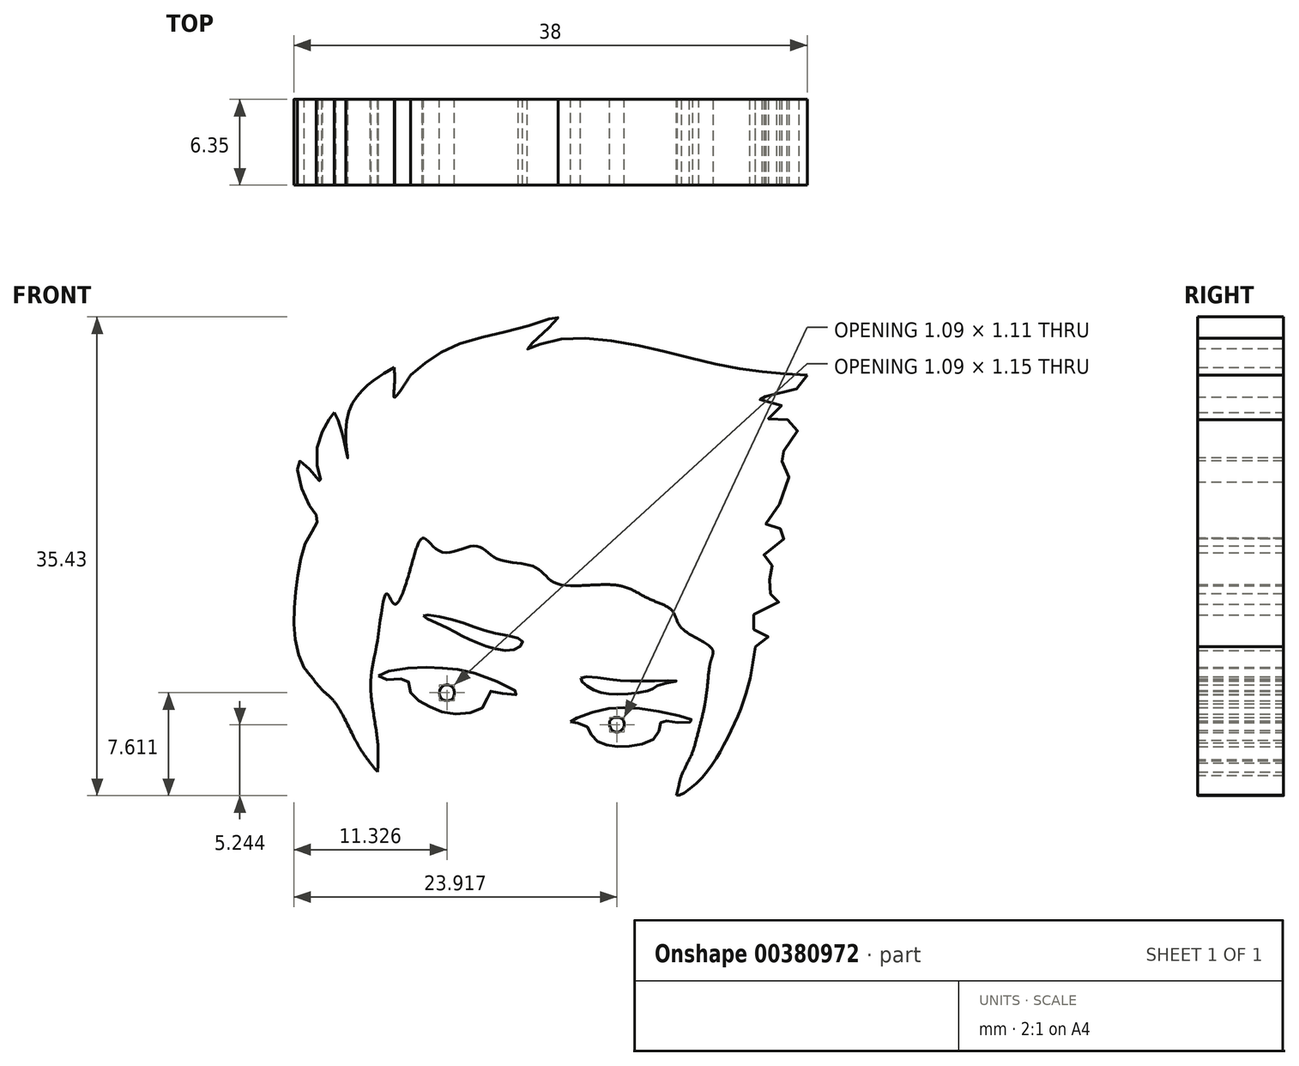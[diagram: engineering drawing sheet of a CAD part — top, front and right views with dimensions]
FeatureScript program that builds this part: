
annotation { "Feature Type Name" : "Feature", "Feature Type Description" : "" }
export const myFeature = defineFeature(function(context is Context, id is Id, definition is map)
    precondition{}
    {
        {
            var Q0;
            Q0=qCreatedBy(makeId("Front.planeOp"),FACE);
            var sketch = newSketch(context, id + "F0", { "sketchPlane" : qUnion([Q0])});
            skFitSpline(sketch, "E0", {"points": [v(-95.52, 0) * mm, v(-96.95, 1.96) * mm, v(-98.6, 5.04) * mm, v(-99.58, 6.02) * mm, v(-100.94, 7.67) * mm, v(-101.69, 10.58) * mm, v(-101.5, 13.97) * mm, v(-100.7, 17.24) * mm, v(-99.94, 18.67) * mm, v(-100.75, 20.01) * mm, v(-101.29, 23) * mm, v(-99.72, 21.44) * mm, v(-100.04, 23.01) * mm, v(-99.1, 26.1) * mm, v(-98.57, 26.77) * mm], "startDerivative": vector(-19.5, 23.13) * mm, "endDerivative": vector(11.06, 11.7) * mm});
            skFitSpline(sketch, "E1", {"points": [v(-98.73, 26.6) * mm, v(-98.23, 25.4) * mm, v(-97.73, 23.23) * mm, v(-97.79, 26.1) * mm, v(-95.96, 28.85) * mm, v(-94.28, 29.93) * mm], "startDerivative": vector(3.2, -5.81) * mm, "endDerivative": vector(8.73, 4.96) * mm});
            skFitSpline(sketch, "E2", {"points": [v(-94.28, 29.93) * mm, v(-94.28, 28.47) * mm, v(-94.28, 27.72) * mm, v(-93.08, 29.36) * mm], "startDerivative": vector(0.17, -4.17) * mm, "endDerivative": vector(3.9, 6.25) * mm});
            skFitSpline(sketch, "E3", {"points": [v(-93.08, 29.36) * mm, v(-89.77, 31.56) * mm, v(-84.03, 33.1) * mm, v(-82.17, 33.58) * mm, v(-84.45, 31.34) * mm, v(-82.96, 31.82) * mm, v(-76.32, 31.56) * mm, v(-69.24, 29.93) * mm, v(-63.71, 29.36) * mm], "startDerivative": vector(24.23, 20.38) * mm, "endDerivative": vector(37.72, -2.28) * mm});
            skFitSpline(sketch, "E4", {"points": [v(-93.6, 28.51) * mm, v(-93.08, 29.36) * mm, v(-92.1, 30.18) * mm], "startDerivative": vector(0.96, 1.87) * mm, "endDerivative": vector(2.03, 1.48) * mm});
            skFitSpline(sketch, "E5", {"points": [v(-95.52, 0) * mm, v(-95.52, 2.32) * mm, v(-96.03, 6.34) * mm, v(-95.52, 9.78) * mm, v(-94.82, 13.18) * mm, v(-94.28, 12.42) * mm, v(-93.08, 15.06) * mm, v(-92.1, 17.3) * mm, v(-90.76, 16.27) * mm, v(-88.25, 16.71) * mm, v(-86.69, 15.78) * mm, v(-83.87, 15.15) * mm, v(-82.26, 13.94) * mm, v(-77.79, 13.8) * mm, v(-75.46, 12.82) * mm, v(-73.72, 11.93) * mm, v(-73, 10.63) * mm, v(-70.77, 9.11) * mm, v(-70.86, 8.17) * mm, v(-71.22, 5.45) * mm, v(-72.29, 1.24) * mm], "startDerivative": vector(2.92, 43.61) * mm, "endDerivative": vector(-19.8, -65.15) * mm});
            skFitSpline(sketch, "E6", {"points": [v(-72.29, 1.24) * mm, v(-73.4, -1.74) * mm, v(-71.6, -0.53) * mm, v(-69.69, 2.38) * mm, v(-68.26, 5.73) * mm, v(-67.54, 9.26) * mm], "startDerivative": vector(-10.39, -20.95) * mm, "endDerivative": vector(2.54, 16.76) * mm});
            skFitSpline(sketch, "E7", {"points": [v(-63.71, 29.36) * mm, v(-64.65, 28.27) * mm, v(-67.58, 27.6) * mm, v(-65.62, 27.15) * mm, v(-66.6, 26.1) * mm, v(-64.57, 25.94) * mm, v(-64.8, 24.59) * mm, v(-65.77, 23.16) * mm, v(-65.32, 22.79) * mm, v(-65.47, 20.3) * mm, v(-66.75, 18.2) * mm, v(-65.4, 17.9) * mm, v(-65.4, 17.3) * mm, v(-67.05, 15.72) * mm, v(-66, 14.96) * mm, v(-66.9, 13.54) * mm, v(-65.62, 12.78) * mm, v(-67.8, 11.5) * mm, v(-67.65, 10.53) * mm, v(-66.6, 10) * mm, v(-67.54, 9.26) * mm], "startDerivative": vector(-8.06, -25.32) * mm, "endDerivative": vector(-34.73, -19.36) * mm});
            skFitSpline(sketch, "E8", {"points": [v(-100.94, 7.67) * mm, v(-101.6, 8.1) * mm, v(-102.13, 7.03) * mm, v(-102.24, 4.16) * mm, v(-100.94, 1.6) * mm, v(-99.36, 0) * mm, v(-96.97, -0.84) * mm, v(-96.01, -2.7) * mm, v(-93.46, -4.77) * mm, v(-89.95, -7.22) * mm, v(-88.1, -7.22) * mm, v(-87.99, -7.9) * mm, v(-85.38, -8.76) * mm, v(-81.02, -8.5) * mm, v(-80.28, -8.28) * mm, v(-79.8, -7.11) * mm, v(-78.79, -8.07) * mm, v(-75.97, -6.31) * mm, v(-74.16, -3.5) * mm, v(-73.4, -1.74) * mm, v(-72.98, -0.15) * mm, v(-72.29, 1.24) * mm, v(-71.85, 2.68) * mm, v(-71.22, 5.45) * mm, v(-70.86, 8.17) * mm, v(-70.77, 9.11) * mm, v(-73, 10.63) * mm, v(-73.72, 11.93) * mm, v(-75.46, 12.82) * mm, v(-77.79, 13.8) * mm, v(-82.26, 13.94) * mm, v(-83.87, 15.15) * mm, v(-86.69, 15.78) * mm, v(-88.25, 16.71) * mm, v(-90.76, 16.27) * mm, v(-92.1, 17.3) * mm, v(-93.08, 15.06) * mm, v(-94.28, 12.42) * mm, v(-94.82, 13.18) * mm, v(-95.52, 9.78) * mm, v(-96.03, 6.34) * mm, v(-95.52, 2.32) * mm, v(-95.47, 0.7) * mm, v(-95.52, 0) * mm, v(-96, 0.57) * mm, v(-96.95, 1.96) * mm, v(-98.6, 5.04) * mm, v(-99.58, 6.02) * mm, v(-100.94, 7.67) * mm]});
            skFitSpline(sketch, "E9", {"points": [v(-92.13, 11.55) * mm, v(-89.85, 11.24) * mm, v(-87, 10.3) * mm, v(-84.8, 9.66) * mm, v(-85.23, 9.09) * mm, v(-87.2, 9.22) * mm, v(-88.96, 9.91) * mm, v(-90.55, 10.73) * mm, v(-92.13, 11.55) * mm]});
            skFitSpline(sketch, "E10", {"points": [v(-80.46, 6.96) * mm, v(-78.33, 6.85) * mm, v(-75.65, 6.72) * mm, v(-73.34, 6.72) * mm, v(-74.83, 6.37) * mm, v(-75.3, 6.05) * mm, v(-77.46, 5.76) * mm, v(-79.08, 5.9) * mm, v(-80.22, 6.5) * mm, v(-80.46, 6.96) * mm]});
            skFitSpline(sketch, "E11", {"points": [v(-95.44, 7.1) * mm, v(-93.45, 7.67) * mm, v(-90.63, 7.67) * mm, v(-88, 7.18) * mm, v(-85.1, 5.8) * mm, v(-86.2, 5.8) * mm, v(-87.28, 5.9) * mm, v(-87.5, 5.04) * mm, v(-88.75, 4.36) * mm, v(-90.63, 4.4) * mm, v(-92.06, 5.04) * mm, v(-93.07, 5.87) * mm, v(-93.3, 6.8) * mm, v(-94.54, 6.8) * mm, v(-95.44, 7.1) * mm]});
            skFitSpline(sketch, "E12", {"points": [v(-90.74, 6.32) * mm, v(-90.82, 5.45) * mm, v(-90.06, 5.34) * mm, v(-89.84, 5.8) * mm, v(-90.03, 6.32) * mm, v(-90.74, 6.32) * mm]});
            skFitSpline(sketch, "E13", {"points": [v(-81.23, 3.7) * mm, v(-79.1, 4.53) * mm, v(-75.55, 4.61) * mm, v(-72.19, 3.78) * mm, v(-73.49, 3.67) * mm, v(-74.51, 3.7) * mm, v(-74.8, 2.69) * mm, v(-76.6, 1.93) * mm, v(-78.45, 1.96) * mm, v(-79.56, 2.53) * mm, v(-80.16, 3.46) * mm, v(-81.23, 3.7) * mm]});
            skFitSpline(sketch, "E14", {"points": [v(-78.26, 3.87) * mm, v(-77.47, 3.95) * mm, v(-77.28, 3.35) * mm, v(-77.77, 2.93) * mm, v(-78.22, 3.16) * mm, v(-78.26, 3.87) * mm]});
            skFitSpline(sketch, "E15", {"points": [v(-83.13, 2.17) * mm, v(-83.45, 1.19) * mm, v(-83.63, 0) * mm, v(-83.18, 0) * mm, v(-83.22, 1.1) * mm, v(-83.13, 2.17) * mm]});
            skFitSpline(sketch, "E16", {"points": [v(-87.52, -3.15) * mm, v(-85.37, -3.06) * mm, v(-82.24, -2.8) * mm, v(-81.4, -2.93) * mm, v(-81.88, -3.64) * mm, v(-83.18, -4.72) * mm, v(-84.65, -4.76) * mm, v(-86.18, -4.27) * mm, v(-87.52, -3.15) * mm]});
            skFitSpline(sketch, "E17", {"points": [v(-85.72, -4.48) * mm, v(-85.82, -3.05) * mm], "startDerivative": vector(-0.1, 1.44) * mm, "endDerivative": vector(-0.1, 1.44) * mm});
            skFitSpline(sketch, "E18", {"points": [v(-84.08, -3) * mm, v(-84.07, -4.83) * mm], "startDerivative": vector(0, -1.85) * mm, "endDerivative": vector(0, -1.85) * mm});
            skFitSpline(sketch, "E19", {"points": [v(-82.69, -2.83) * mm, v(-82.6, -4.35) * mm], "startDerivative": vector(0.1, -1.52) * mm, "endDerivative": vector(0.1, -1.52) * mm});
            skSolve(sketch);
        }
        {
            var Q0;
            {var subQ1=sQuery(id+"F0.wireOp",EDGE,"E3");Q0=makeQuery(id+"F0.imprint","IMPRINT",FACE,{"disambiguationData":[TD([[makeQuery(id+"F0.imprint","IMPRINT",EDGE,{"derivedFrom":subQ1}),-1.0]])]});}
            extrude(context, id + "F1", {"entities" : qUnion([Q0]), "depth" : 6.35 * mm});
        }
        {
            var Q0;
            Q0=makeQuery(id+"F0.imprint","IMPRINT",FACE,{"disambiguationData":[TD([[makeQuery(id+"F0.imprint","IMPRINT",EDGE,{"derivedFrom":sQuery(id+"F0.wireOp",EDGE,"E9")}),-1.0]])]});
            var Q1;
            Q1=makeQuery(id+"F0.imprint","IMPRINT",FACE,{"disambiguationData":[TD([[makeQuery(id+"F0.imprint","IMPRINT",EDGE,{"derivedFrom":sQuery(id+"F0.wireOp",EDGE,"E10")}),-1.0]])]});
            var Q2;
            Q2=makeQuery(id+"F0.imprint","IMPRINT",FACE,{"disambiguationData":[TD([[makeQuery(id+"F0.imprint","IMPRINT",EDGE,{"derivedFrom":sQuery(id+"F0.wireOp",EDGE,"E11")}),-1.0]])]});
            var Q3;
            Q3=makeQuery(id+"F0.imprint","IMPRINT",FACE,{"disambiguationData":[TD([[makeQuery(id+"F0.imprint","IMPRINT",EDGE,{"derivedFrom":sQuery(id+"F0.wireOp",EDGE,"E13")}),-1.0]])]});
            extrude(context, id + "F2", {"entities" : qUnion([Q0, Q1, Q2, Q3]), "depth" : 6.35 * mm});
        }
        {
            var Q0;
            Q0=sQuery(id+"F0.wireOp",EDGE,"E15");
            extrude(context, id + "F3", {"bodyType" : ToolBodyType.SURFACE, "surfaceEntities" : qUnion([Q0]), "depth" : 6.35 * mm});
        }
    });
